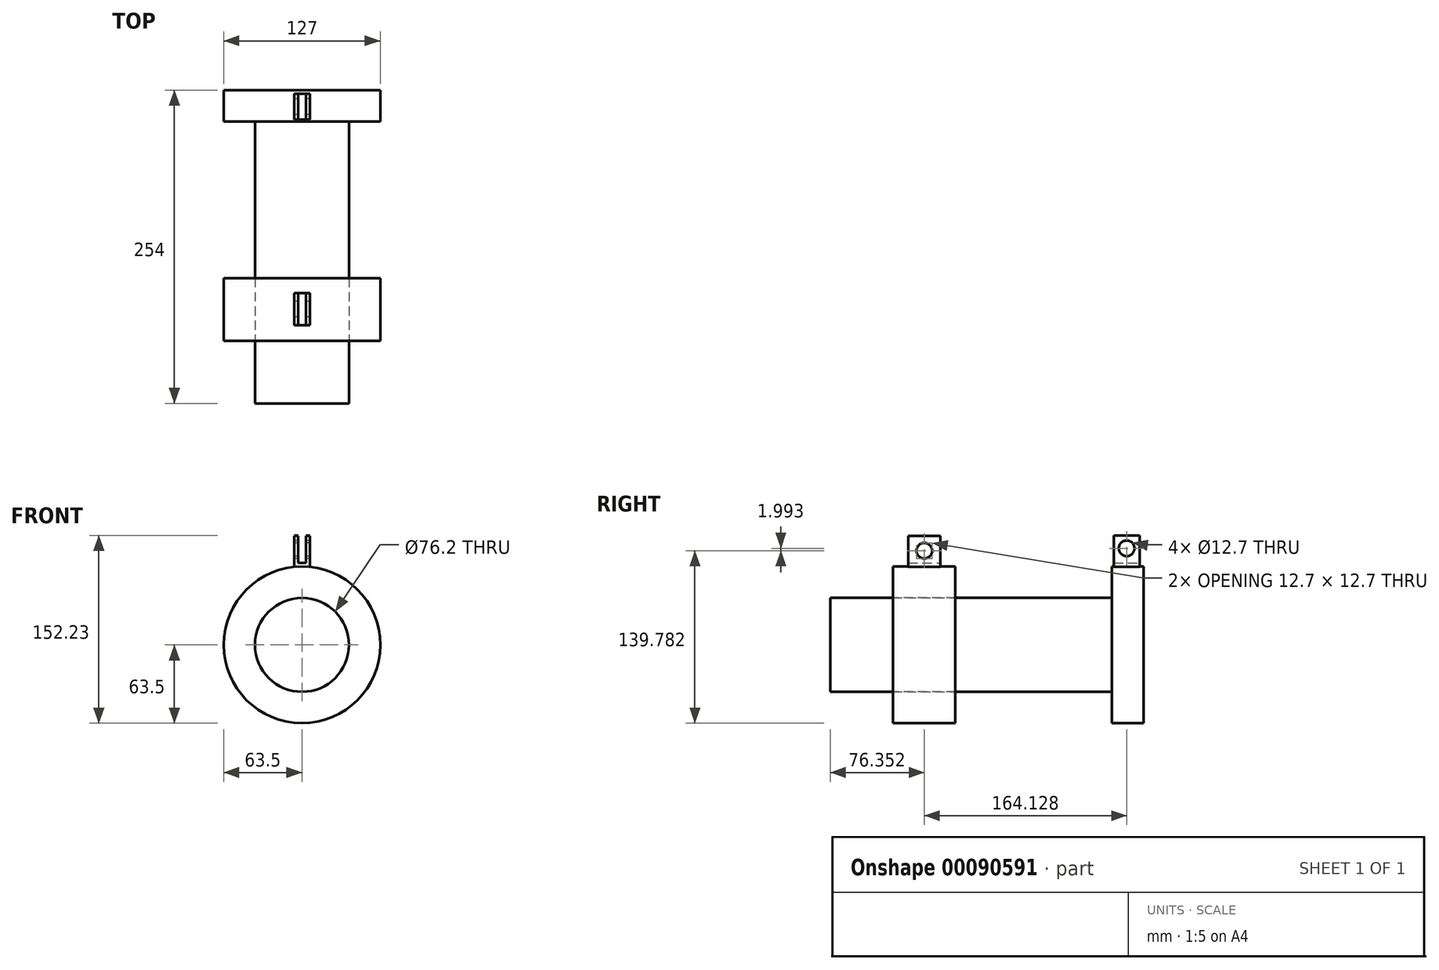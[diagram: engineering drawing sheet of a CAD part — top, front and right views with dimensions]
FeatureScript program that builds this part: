
annotation { "Feature Type Name" : "Feature", "Feature Type Description" : "" }
export const myFeature = defineFeature(function(context is Context, id is Id, definition is map)
    precondition{}
    {
        {
            var Q0;
            Q0=qCreatedBy(makeId("Front.planeOp"),FACE);
            var sketch = newSketch(context, id + "F0", { "sketchPlane" : qUnion([Q0])});
            skCircle(sketch, "E0", {"center": v(0, 0) * mm, "radius": 38.1 * mm});
            skSolve(sketch);
        }
        {
            var Q0;
            Q0=makeQuery(id+"F0.imprint","IMPRINT",FACE,{"disambiguationData":[TD([[makeQuery(id+"F0.imprint","IMPRINT",EDGE,{"derivedFrom":sQuery(id+"F0.wireOp",EDGE,"E0")}),1.0]])]});
            extrude(context, id + "F1", {"entities" : qUnion([Q0]), "depth" : 254 * mm});
        }
        {
            var Q0;
            Q0=makeQuery(id+"F1.opExtrude","CAP_FACE",FACE,{"disambiguationData":[OSD([sQuery(id+"F0.wireOp",EDGE,"E0")])],"isStart":true});
            var sketch = newSketch(context, id + "F2", { "sketchPlane" : qUnion([Q0])});
            skCircle(sketch, "E1", {"center": v(0, 0) * mm, "radius": 63.5 * mm});
            skSolve(sketch);
        }
        {
            var Q0;
            Q0 = qSketchRegion(id + "F2", true);
            extrude(context, id + "F3", {"entities" : qUnion([Q0]), "operationType" : NewBodyOperationType.ADD, "oppositeDirection" : true, "depth" : 25.4 * mm});
        }
        {
            var Q0;
            Q0=makeQuery(id+"F1.opExtrude","CAP_FACE",FACE,{"disambiguationData":[OSD([sQuery(id+"F0.wireOp",EDGE,"E0")])],"isStart":false});
            var sketch = newSketch(context, id + "F4", { "sketchPlane" : qUnion([Q0])});
            skCircle(sketch, "E2", {"center": v(0, 0) * mm, "radius": 38.1 * mm});
            skCircle(sketch, "E3", {"center": v(0, 0) * mm, "radius": 63.5 * mm});
            skSolve(sketch);
        }
        {
            var Q0;
            Q0=makeQuery(id+"F4.imprint","IMPRINT",FACE,{"disambiguationData":[TD([[makeQuery(id+"F4.imprint","IMPRINT",EDGE,{"derivedFrom":sQuery(id+"F4.wireOp",EDGE,"E2")}),-1.0]])]});
            extrude(context, id + "F5", {"entities" : qUnion([Q0]), "oppositeDirection" : true, "depth" : 50.8 * mm});
        }
        {
            var Q0;
            Q0=makeQuery(id+"F5.opExtrude","SWEPT_BODY",BODY,{"disambiguationData":[OSD([sQuery(id+"F4.wireOp",EDGE,"E2"),sQuery(id+"F4.wireOp",EDGE,"E3")])]});
            var Q1;
            Q1=makeQuery(id+"F1.opExtrude","SWEPT_FACE",FACE,{"disambiguationData":[OSD([sQuery(id+"F0.wireOp",EDGE,"E0")])]});
            transform(context, id + "F6", {"entities" : qUnion([Q0]), "transformType" : TransformType.TRANSLATION_DISTANCE, "transformDirection" : qUnion([Q1]), "distance" : 50.8 * mm, "makeCopy" : false});
        }
        {
            var Q0;
            Q0=qCreatedBy(makeId("Right.planeOp"),FACE);
            var sketch = newSketch(context, id + "F7", { "sketchPlane" : qUnion([Q0])});
            skLineSegment(sketch, "E4", {"start": v(-190.61, 49.97) * mm, "end": v(-190.61, 88.18) * mm});
            skLineSegment(sketch, "E5", {"start": v(-190.61, 88.18) * mm, "end": v(-164.69, 88.18) * mm});
            skLineSegment(sketch, "E6", {"start": v(-164.69, 88.18) * mm, "end": v(-164.69, 49.97) * mm});
            skCircle(sketch, "E7", {"center": v(-177.65, 76.28) * mm, "radius": 6.35 * mm});
            skPoint(sketch, "E7.centerSnap0", {"position": v(-177.65, 88.18) * mm});
            skLineSegment(sketch, "E8", {"start": v(-190.61, 49.97) * mm, "end": v(-164.69, 49.97) * mm});
            skSolve(sketch);
        }
        {
            var Q0;
            Q0=makeQuery(id+"F7.imprint","IMPRINT",FACE,{"disambiguationData":[TD([[makeQuery(id+"F7.imprint","IMPRINT",EDGE,{"derivedFrom":sQuery(id+"F7.wireOp",EDGE,"E4")}),-1.0]])]});
            extrude(context, id + "F8", {"entities" : qUnion([Q0]), "operationType" : NewBodyOperationType.ADD, "endBound" : BoundingType.SYMMETRIC, "depth" : 12.7 * mm});
        }
        {
            var Q0;
            Q0=qCreatedBy(makeId("Right.planeOp"),FACE);
            var sketch = newSketch(context, id + "F9", { "sketchPlane" : qUnion([Q0])});
            skLineSegment(sketch, "E9", {"start": v(-23.93, 52.98) * mm, "end": v(-23.93, 88.73) * mm});
            skLineSegment(sketch, "E10", {"start": v(-23.93, 88.73) * mm, "end": v(-3.1, 88.73) * mm});
            skLineSegment(sketch, "E11", {"start": v(-3.1, 88.73) * mm, "end": v(-3.1, 52.98) * mm});
            skLineSegment(sketch, "E12", {"start": v(-23.93, 52.98) * mm, "end": v(-3.1, 52.98) * mm});
            skPoint(sketch, "E13.orphan", {"position": v(-3.1, 52.2) * mm});
            skCircle(sketch, "E14", {"center": v(-13.52, 78.28) * mm, "radius": 6.35 * mm});
            skPoint(sketch, "E14.centerSnap0", {"position": v(-13.52, 88.73) * mm});
            skSolve(sketch);
        }
        {
            var Q0;
            Q0=makeQuery(id+"F9.imprint","IMPRINT",FACE,{"disambiguationData":[TD([[makeQuery(id+"F9.imprint","IMPRINT",EDGE,{"derivedFrom":sQuery(id+"F9.wireOp",EDGE,"E9")}),-1.0]])]});
            extrude(context, id + "F10", {"entities" : qUnion([Q0]), "operationType" : NewBodyOperationType.ADD, "endBound" : BoundingType.SYMMETRIC, "depth" : 12.7 * mm});
        }
        {
            var Q0;
            Q0=qCreatedBy(makeId("Front.planeOp"),FACE);
            var sketch = newSketch(context, id + "F11", { "sketchPlane" : qUnion([Q0])});
            skLineSegment(sketch, "E15", {"start": v(0, 66.43) * mm, "end": v(0, 90.22) * mm, "construction": true});
            skLineSegment(sketch, "E16", {"start": v(0, 66.43) * mm, "end": v(-3.18, 66.43) * mm});
            skLineSegment(sketch, "E17", {"start": v(-3.18, 66.43) * mm, "end": v(-3.18, 90.22) * mm});
            skLineSegment(sketch, "E18", {"start": v(-3.18, 90.22) * mm, "end": v(0, 90.22) * mm});
            skLineSegment(sketch, "E19.MirrorCS", {"start": v(3.18, 90.22) * mm, "end": v(0, 90.22) * mm});
            skLineSegment(sketch, "E20.MirrorCS", {"start": v(3.18, 66.43) * mm, "end": v(3.18, 90.22) * mm});
            skLineSegment(sketch, "E21.MirrorCS", {"start": v(0, 66.43) * mm, "end": v(3.18, 66.43) * mm});
            skSolve(sketch);
        }
        {
            var Q0;
            Q0=makeQuery(id+"F11.imprint","IMPRINT",FACE,{"disambiguationData":[TD([[makeQuery(id+"F11.imprint","IMPRINT",EDGE,{"derivedFrom":sQuery(id+"F11.wireOp",EDGE,"E16")}),-1.0]])]});
            extrude(context, id + "F12", {"entities" : qUnion([Q0]), "operationType" : NewBodyOperationType.REMOVE, "depth" : 254 * mm});
        }
    });
